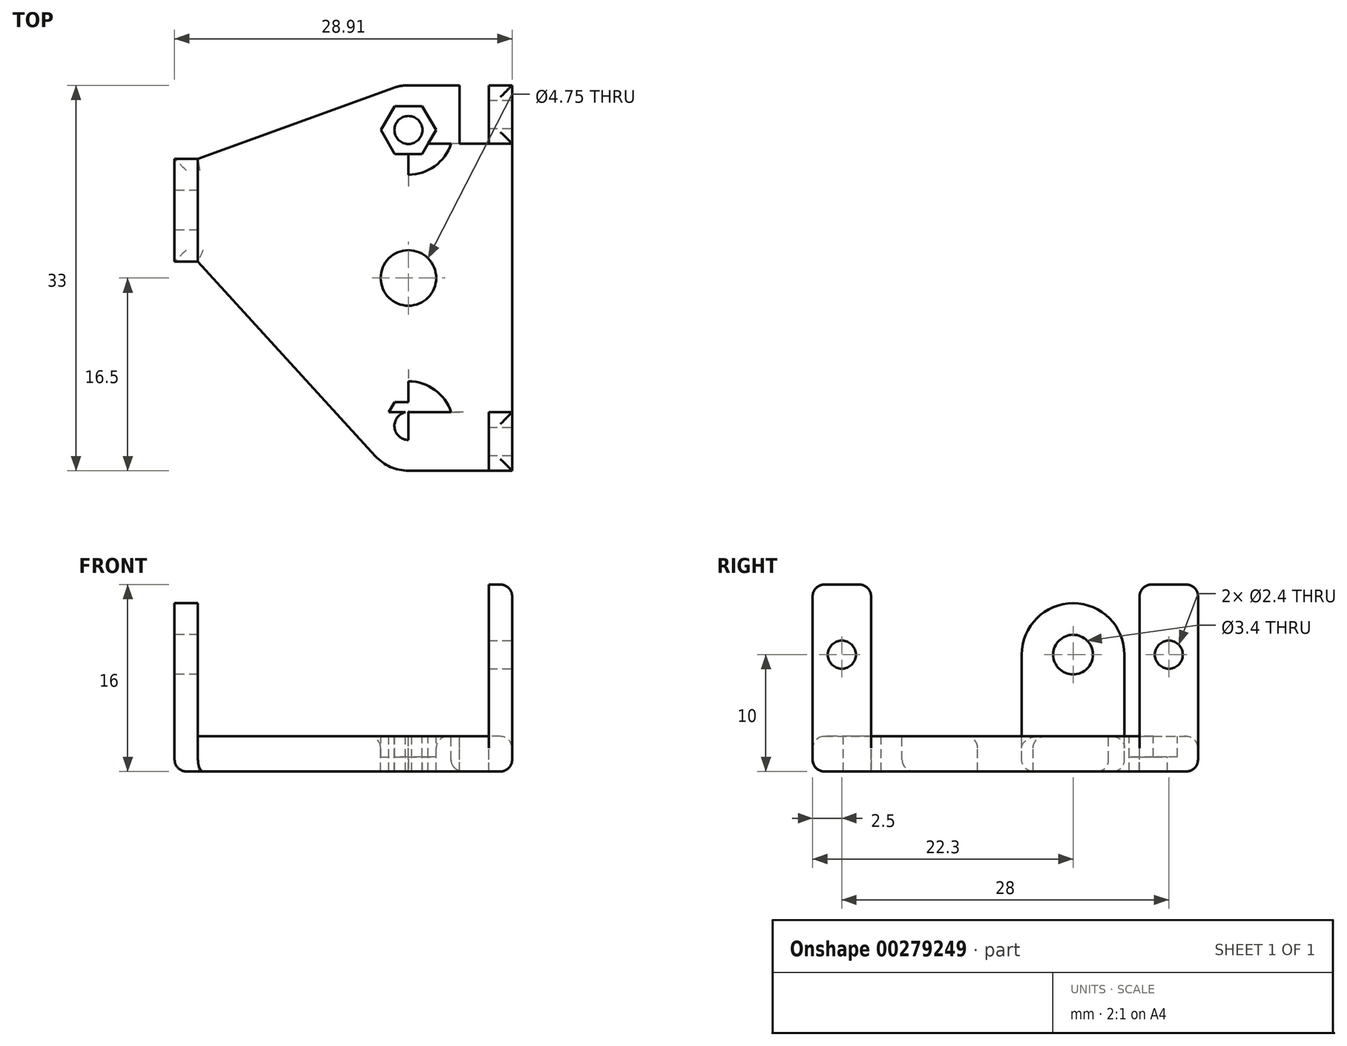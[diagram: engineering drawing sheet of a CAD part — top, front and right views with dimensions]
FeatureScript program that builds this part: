
annotation { "Feature Type Name" : "Feature", "Feature Type Description" : "" }
export const myFeature = defineFeature(function(context is Context, id is Id, definition is map)
    precondition{}
    {
        {
            var Q0;
            Q0=qCreatedBy(makeId("Top.planeOp"),FACE);
            var sketch = newSketch(context, id + "F0", { "sketchPlane" : qUnion([Q0])});
            skPoint(sketch, "E0.middle", {"position": v(0, 0) * mm});
            skCircle(sketch, "E1", {"center": v(0, 0) * mm, "radius": 2.38 * mm});
            skCircle(sketch, "E2", {"center": v(0, 12.67) * mm, "radius": 1.2 * mm});
            skCircle(sketch, "E3.MirrorC", {"center": v(0, -12.67) * mm, "radius": 1.2 * mm});
            skLineSegment(sketch, "E4.bottom", {"start": v(11.38, -11.5) * mm, "end": v(-11.38, -11.5) * mm});
            skLineSegment(sketch, "E4.top", {"start": v(11.38, 11.5) * mm, "end": v(-11.38, 11.5) * mm});
            skLineSegment(sketch, "E4.left", {"start": v(11.38, -11.5) * mm, "end": v(11.38, 11.5) * mm});
            skLineSegment(sketch, "E4.right", {"start": v(-11.38, -11.5) * mm, "end": v(-11.37, 11.5) * mm});
            skLineSegment(sketch, "E5.bottom", {"start": v(6.87, 11.5) * mm, "end": v(4.38, 11.5) * mm});
            skLineSegment(sketch, "E5.top", {"start": v(6.87, 16.5) * mm, "end": v(4.37, 16.5) * mm});
            skLineSegment(sketch, "E5.left", {"start": v(6.87, 11.5) * mm, "end": v(6.87, 16.5) * mm});
            skLineSegment(sketch, "E5.right", {"start": v(4.37, 11.5) * mm, "end": v(4.37, 16.5) * mm});
            skLineSegment(sketch, "E6.MirrorCS", {"start": v(4.38, -11.5) * mm, "end": v(4.38, -16.5) * mm});
            skLineSegment(sketch, "E7.MirrorCS", {"start": v(6.87, -11.5) * mm, "end": v(4.38, -11.5) * mm});
            skLineSegment(sketch, "E8.MirrorCS", {"start": v(6.88, -11.5) * mm, "end": v(6.88, -16.5) * mm});
            skLineSegment(sketch, "E9.MirrorCS", {"start": v(6.87, -16.5) * mm, "end": v(4.37, -16.5) * mm});
            skLineSegment(sketch, "E10.bottom", {"start": v(11.38, 11.5) * mm, "end": v(15.62, 11.5) * mm});
            skLineSegment(sketch, "E10.top", {"start": v(11.37, -0.5) * mm, "end": v(15.62, -0.5) * mm});
            skLineSegment(sketch, "E10.left", {"start": v(11.38, 11.5) * mm, "end": v(11.38, -0.5) * mm});
            skLineSegment(sketch, "E10.right", {"start": v(15.62, 11.5) * mm, "end": v(15.62, -0.5) * mm});
            skLineSegment(sketch, "E11.bottom", {"start": v(15.62, 8.1) * mm, "end": v(18.63, 8.1) * mm});
            skLineSegment(sketch, "E11.top", {"start": v(15.62, 3.5) * mm, "end": v(18.63, 3.5) * mm});
            skLineSegment(sketch, "E11.left", {"start": v(15.62, 8.1) * mm, "end": v(15.62, 3.5) * mm});
            skLineSegment(sketch, "E11.right", {"start": v(18.62, 8.1) * mm, "end": v(18.62, 3.5) * mm});
            skCircle(sketch, "E12.cCircle", {"center": v(0, 12.67) * mm, "radius": 2.05 * mm, "construction": true});
            skLineSegment(sketch, "E12.0", {"start": v(1.18, 10.62) * mm, "end": v(-1.18, 10.62) * mm});
            skLineSegment(sketch, "E12.1", {"start": v(-1.18, 10.62) * mm, "end": v(-2.37, 12.67) * mm});
            skLineSegment(sketch, "E12.2", {"start": v(-2.37, 12.67) * mm, "end": v(-1.18, 14.72) * mm});
            skLineSegment(sketch, "E12.3", {"start": v(-1.18, 14.72) * mm, "end": v(1.18, 14.72) * mm});
            skLineSegment(sketch, "E12.4", {"start": v(1.18, 14.72) * mm, "end": v(2.37, 12.67) * mm});
            skLineSegment(sketch, "E12.5", {"start": v(2.37, 12.67) * mm, "end": v(1.18, 10.62) * mm});
            skPoint(sketch, "E12.0.midPoint", {"position": v(0, 10.62) * mm});
            skCircle(sketch, "E13.MirrorC", {"center": v(0, -12.67) * mm, "radius": 2.05 * mm, "construction": true});
            skLineSegment(sketch, "E14.MirrorCS", {"start": v(1.18, -10.62) * mm, "end": v(-1.18, -10.62) * mm});
            skLineSegment(sketch, "E15.MirrorCS", {"start": v(2.37, -12.67) * mm, "end": v(1.18, -10.62) * mm});
            skLineSegment(sketch, "E16.MirrorCS", {"start": v(1.18, -14.72) * mm, "end": v(2.37, -12.67) * mm});
            skLineSegment(sketch, "E17.MirrorCS", {"start": v(-1.18, -14.72) * mm, "end": v(1.18, -14.72) * mm});
            skLineSegment(sketch, "E18.MirrorCS", {"start": v(-2.37, -12.67) * mm, "end": v(-1.18, -14.72) * mm});
            skLineSegment(sketch, "E19.MirrorCS", {"start": v(-1.18, -10.62) * mm, "end": v(-2.37, -12.67) * mm});
            skLineSegment(sketch, "E20.bottom", {"start": v(20.62, 24.4) * mm, "end": v(-20.62, 24.4) * mm});
            skLineSegment(sketch, "E20.top", {"start": v(20.62, 26.4) * mm, "end": v(-20.62, 26.4) * mm});
            skLineSegment(sketch, "E20.left", {"start": v(20.63, 24.4) * mm, "end": v(20.63, 26.4) * mm});
            skLineSegment(sketch, "E20.right", {"start": v(-20.63, 24.4) * mm, "end": v(-20.63, 26.4) * mm});
            skPoint(sketch, "E20.middle", {"position": v(0, 25.4) * mm});
            skLineSegment(sketch, "E21.bottom", {"start": v(22.62, 1.4) * mm, "end": v(20.62, 1.4) * mm});
            skLineSegment(sketch, "E21.top", {"start": v(22.62, 26.4) * mm, "end": v(20.62, 26.4) * mm});
            skLineSegment(sketch, "E21.left", {"start": v(22.62, 1.4) * mm, "end": v(22.62, 26.4) * mm});
            skLineSegment(sketch, "E21.right", {"start": v(20.62, 1.4) * mm, "end": v(20.62, 26.4) * mm});
            skLineSegment(sketch, "E22.MirrorCS", {"start": v(-22.62, 26.4) * mm, "end": v(-20.62, 26.4) * mm});
            skLineSegment(sketch, "E23.MirrorCS", {"start": v(-20.62, 1.4) * mm, "end": v(-20.62, 26.4) * mm});
            skLineSegment(sketch, "E24.MirrorCS", {"start": v(-22.62, 1.4) * mm, "end": v(-22.62, 26.4) * mm});
            skLineSegment(sketch, "E25.MirrorCS", {"start": v(-22.62, 1.4) * mm, "end": v(-20.62, 1.4) * mm});
            skCircle(sketch, "E26", {"center": v(0, 12.67) * mm, "radius": 3.83 * mm});
            skPoint(sketch, "E27.firstSnap0", {"position": v(0, 24.4) * mm});
            skLineSegment(sketch, "E27.bottom", {"start": v(0, 16.5) * mm, "end": v(8.87, 16.5) * mm});
            skLineSegment(sketch, "E27.top", {"start": v(0, -16.5) * mm, "end": v(8.88, -16.5) * mm});
            skLineSegment(sketch, "E27.left", {"start": v(0, 16.5) * mm, "end": v(0, -16.5) * mm});
            skLineSegment(sketch, "E27.right", {"start": v(8.87, 16.5) * mm, "end": v(8.88, -16.5) * mm});
            skCircle(sketch, "E28.MirrorC", {"center": v(0, -12.67) * mm, "radius": 3.83 * mm});
            skLineSegment(sketch, "E29.bottom", {"start": v(-20.62, 9.2) * mm, "end": v(-20.02, 9.2) * mm});
            skLineSegment(sketch, "E29.top", {"start": v(-20.62, 2.4) * mm, "end": v(-20.02, 2.4) * mm});
            skLineSegment(sketch, "E29.left", {"start": v(-20.62, 9.2) * mm, "end": v(-20.62, 2.4) * mm});
            skLineSegment(sketch, "E29.right", {"start": v(-20.02, 9.2) * mm, "end": v(-20.02, 2.4) * mm});
            skLineSegment(sketch, "E30.bottom", {"start": v(-18.02, 10.2) * mm, "end": v(-20.02, 10.2) * mm});
            skLineSegment(sketch, "E30.top", {"start": v(-18.02, 1.4) * mm, "end": v(-20.02, 1.4) * mm});
            skLineSegment(sketch, "E30.left", {"start": v(-18.02, 10.2) * mm, "end": v(-18.02, 1.4) * mm});
            skLineSegment(sketch, "E30.right", {"start": v(-20.02, 10.2) * mm, "end": v(-20.02, 1.4) * mm});
            skLineSegment(sketch, "E31", {"start": v(-18.02, 10.2) * mm, "end": v(-1.3, 16.27) * mm});
            skLineSegment(sketch, "E32", {"start": v(-18.02, 1.4) * mm, "end": v(-2.83, -15.25) * mm});
            skPoint(sketch, "E33.startSnap0", {"position": v(18.62, 5.8) * mm});
            skSolve(sketch);
        }
        {
            var Q0;
            {var subQ2=sQuery(id+"F0.wireOp",EDGE,"E30.bottom");Q0=makeQuery(id+"F0.imprint","IMPRINT",FACE,{"disambiguationData":[TD([[makeQuery(id+"F0.imprint","IMPRINT",EDGE,{"derivedFrom":subQ2}),1.0]])]});}
            var Q1;
            {var subQ0=sQuery(id+"F0.wireOp",EDGE,"E30.left");Q1=makeQuery(id+"F0.imprint","IMPRINT",FACE,{"disambiguationData":[TD([[makeQuery(id+"F0.imprint","IMPRINT",EDGE,{"derivedFrom":subQ0}),1.0]])]});}
            var Q2;
            {var subQ5=sQuery(id+"F0.wireOp",EDGE,"E27.left");var subQ6=sQuery(id+"F0.wireOp",EDGE,"E1");var subQ7=makeQuery(id+"F0.imprint","INTERSECT",VERTEX,{"disambiguationData":[OD(0.0)],"derivedFrom":[subQ6,subQ5]});Q2=makeQuery(id+"F0.imprint","IMPRINT",FACE,{"disambiguationData":[TD([[makeQuery(id+"F0.imprint","IMPRINT",EDGE,{"disambiguationData":[TD([[subQ7,-1.0]])],"derivedFrom":subQ6}),-1.0]])]});}
            var Q3;
            {var subQ0=sQuery(id+"F0.wireOp",EDGE,"E12.2");Q3=makeQuery(id+"F0.imprint","IMPRINT",FACE,{"disambiguationData":[TD([[makeQuery(id+"F0.imprint","IMPRINT",EDGE,{"derivedFrom":subQ0}),1.0]])]});}
            var Q4;
            {var subQ0=sQuery(id+"F0.wireOp",EDGE,"E12.1");var subQ3=sQuery(id+"F0.wireOp",EDGE,"E4.top");var subQ4=makeQuery(id+"F0.imprint","INTERSECT",VERTEX,{"derivedFrom":[subQ3,subQ0]});Q4=makeQuery(id+"F0.imprint","IMPRINT",FACE,{"disambiguationData":[TD([[makeQuery(id+"F0.imprint","IMPRINT",EDGE,{"disambiguationData":[TD([[subQ4,-1.0]])],"derivedFrom":subQ3}),1.0]])]});}
            var Q5;
            {var subQ0=sQuery(id+"F0.wireOp",EDGE,"E26");var subQ1=sQuery(id+"F0.wireOp",EDGE,"E4.top");var subQ2=makeQuery(id+"F0.imprint","INTERSECT",VERTEX,{"disambiguationData":[OD(0.0)],"derivedFrom":[subQ1,subQ0]});Q5=makeQuery(id+"F0.imprint","IMPRINT",FACE,{"disambiguationData":[TD([[makeQuery(id+"F0.imprint","IMPRINT",EDGE,{"disambiguationData":[TD([[subQ2,-1.0]])],"derivedFrom":subQ1}),1.0]])]});}
            var Q6;
            {var subQ1=sQuery(id+"F0.wireOp",EDGE,"E12.4");Q6=makeQuery(id+"F0.imprint","IMPRINT",FACE,{"disambiguationData":[TD([[makeQuery(id+"F0.imprint","IMPRINT",EDGE,{"derivedFrom":subQ1}),1.0]])]});}
            var Q7;
            {var subQ0=sQuery(id+"F0.wireOp",EDGE,"E5.right");Q7=makeQuery(id+"F0.imprint","IMPRINT",FACE,{"disambiguationData":[TD([[makeQuery(id+"F0.imprint","IMPRINT",EDGE,{"derivedFrom":subQ0}),1.0]])]});}
            var Q8;
            Q8=makeQuery(id+"F0.imprint","IMPRINT",FACE,{"disambiguationData":[TD([[makeQuery(id+"F0.imprint","IMPRINT",EDGE,{"derivedFrom":sQuery(id+"F0.wireOp",EDGE,"E5.bottom")}),-1.0]])]});
            var Q9;
            {var subQ0=sQuery(id+"F0.wireOp",EDGE,"E5.left");Q9=makeQuery(id+"F0.imprint","IMPRINT",FACE,{"disambiguationData":[TD([[makeQuery(id+"F0.imprint","IMPRINT",EDGE,{"derivedFrom":subQ0}),-1.0]])]});}
            var Q10;
            {var subQ10=sQuery(id+"F0.wireOp",EDGE,"E5.bottom");Q10=makeQuery(id+"F0.imprint","IMPRINT",FACE,{"disambiguationData":[TD([[makeQuery(id+"F0.imprint","IMPRINT",EDGE,{"derivedFrom":subQ10}),1.0]])]});}
            var Q11;
            {var subQ0=sQuery(id+"F0.wireOp",EDGE,"E6.MirrorCS");Q11=makeQuery(id+"F0.imprint","IMPRINT",FACE,{"disambiguationData":[TD([[makeQuery(id+"F0.imprint","IMPRINT",EDGE,{"derivedFrom":subQ0}),-1.0]])]});}
            var Q12;
            {var subQ0=sQuery(id+"F0.wireOp",EDGE,"E6.MirrorCS");Q12=makeQuery(id+"F0.imprint","IMPRINT",FACE,{"disambiguationData":[TD([[makeQuery(id+"F0.imprint","IMPRINT",EDGE,{"derivedFrom":subQ0}),1.0]])]});}
            var Q13;
            {var subQ0=sQuery(id+"F0.wireOp",EDGE,"E8.MirrorCS");Q13=makeQuery(id+"F0.imprint","IMPRINT",FACE,{"disambiguationData":[TD([[makeQuery(id+"F0.imprint","IMPRINT",EDGE,{"derivedFrom":subQ0}),1.0]])]});}
            var Q14;
            {var subQ0=sQuery(id+"F0.wireOp",EDGE,"E32");var subQ1=sQuery(id+"F0.wireOp",EDGE,"E4.bottom");var subQ2=makeQuery(id+"F0.imprint","INTERSECT",VERTEX,{"derivedFrom":[subQ1,subQ0]});Q14=makeQuery(id+"F0.imprint","IMPRINT",FACE,{"disambiguationData":[TD([[makeQuery(id+"F0.imprint","IMPRINT",EDGE,{"disambiguationData":[TD([[subQ2,1.0]])],"derivedFrom":subQ1}),1.0]])]});}
            var Q15;
            {var subQ0=sQuery(id+"F0.wireOp",EDGE,"E18.MirrorCS");Q15=makeQuery(id+"F0.imprint","IMPRINT",FACE,{"disambiguationData":[TD([[makeQuery(id+"F0.imprint","IMPRINT",EDGE,{"derivedFrom":subQ0}),-1.0]])]});}
            var Q16;
            {var subQ1=sQuery(id+"F0.wireOp",EDGE,"E16.MirrorCS");Q16=makeQuery(id+"F0.imprint","IMPRINT",FACE,{"disambiguationData":[TD([[makeQuery(id+"F0.imprint","IMPRINT",EDGE,{"derivedFrom":subQ1}),-1.0]])]});}
            var Q17;
            {var subQ5=sQuery(id+"F0.wireOp",EDGE,"E4.bottom");var subQ7=sQuery(id+"F0.wireOp",EDGE,"E19.MirrorCS");var subQ9=makeQuery(id+"F0.imprint","INTERSECT",VERTEX,{"derivedFrom":[subQ5,subQ7]});Q17=makeQuery(id+"F0.imprint","IMPRINT",FACE,{"disambiguationData":[TD([[makeQuery(id+"F0.imprint","IMPRINT",EDGE,{"disambiguationData":[TD([[subQ9,-1.0]])],"derivedFrom":subQ5}),-1.0]])]});}
            var Q18;
            {var subQ3=sQuery(id+"F0.wireOp",EDGE,"E28.MirrorC");var subQ7=sQuery(id+"F0.wireOp",EDGE,"E4.bottom");var subQ9=makeQuery(id+"F0.imprint","INTERSECT",VERTEX,{"disambiguationData":[OD(0.0)],"derivedFrom":[subQ7,subQ3]});Q18=makeQuery(id+"F0.imprint","IMPRINT",FACE,{"disambiguationData":[TD([[makeQuery(id+"F0.imprint","IMPRINT",EDGE,{"disambiguationData":[TD([[subQ9,-1.0]])],"derivedFrom":subQ7}),-1.0]])]});}
            var Q19;
            {var subQ0=sQuery(id+"F0.wireOp",EDGE,"E12.2");Q19=makeQuery(id+"F0.imprint","IMPRINT",FACE,{"disambiguationData":[TD([[makeQuery(id+"F0.imprint","IMPRINT",EDGE,{"derivedFrom":subQ0}),-1.0]])]});}
            var Q20;
            {var subQ0=sQuery(id+"F0.wireOp",EDGE,"E12.4");Q20=makeQuery(id+"F0.imprint","IMPRINT",FACE,{"disambiguationData":[TD([[makeQuery(id+"F0.imprint","IMPRINT",EDGE,{"derivedFrom":subQ0}),-1.0]])]});}
            var Q21;
            {var subQ5=sQuery(id+"F0.wireOp",EDGE,"E2");var subQ7=sQuery(id+"F0.wireOp",EDGE,"E27.left");var subQ9=makeQuery(id+"F0.imprint","INTERSECT",VERTEX,{"disambiguationData":[OD(1.0)],"derivedFrom":[subQ5,subQ7]});Q21=makeQuery(id+"F0.imprint","IMPRINT",FACE,{"disambiguationData":[TD([[makeQuery(id+"F0.imprint","IMPRINT",EDGE,{"disambiguationData":[TD([[subQ9,-1.0]])],"derivedFrom":subQ5}),-1.0]])]});}
            var Q22;
            {var subQ3=sQuery(id+"F0.wireOp",EDGE,"E4.top");var subQ7=sQuery(id+"F0.wireOp",EDGE,"E2");var subQ8=makeQuery(id+"F0.imprint","INTERSECT",VERTEX,{"disambiguationData":[OD(0.0)],"derivedFrom":[subQ7,subQ3]});Q22=makeQuery(id+"F0.imprint","IMPRINT",FACE,{"disambiguationData":[TD([[makeQuery(id+"F0.imprint","IMPRINT",EDGE,{"disambiguationData":[TD([[subQ8,-1.0]])],"derivedFrom":subQ7}),-1.0]])]});}
            var Q23;
            {var subQ0=sQuery(id+"F0.wireOp",EDGE,"E18.MirrorCS");Q23=makeQuery(id+"F0.imprint","IMPRINT",FACE,{"disambiguationData":[TD([[makeQuery(id+"F0.imprint","IMPRINT",EDGE,{"derivedFrom":subQ0}),1.0]])]});}
            var Q24;
            {var subQ5=sQuery(id+"F0.wireOp",EDGE,"E4.bottom");var subQ7=sQuery(id+"F0.wireOp",EDGE,"E3.MirrorC");var subQ8=makeQuery(id+"F0.imprint","INTERSECT",VERTEX,{"disambiguationData":[OD(0.0)],"derivedFrom":[subQ7,subQ5]});Q24=makeQuery(id+"F0.imprint","IMPRINT",FACE,{"disambiguationData":[TD([[makeQuery(id+"F0.imprint","IMPRINT",EDGE,{"disambiguationData":[TD([[subQ8,-1.0]])],"derivedFrom":subQ7}),1.0]])]});}
            var Q25;
            {var subQ0=sQuery(id+"F0.wireOp",EDGE,"E16.MirrorCS");Q25=makeQuery(id+"F0.imprint","IMPRINT",FACE,{"disambiguationData":[TD([[makeQuery(id+"F0.imprint","IMPRINT",EDGE,{"derivedFrom":subQ0}),1.0]])]});}
            var Q26;
            {var subQ5=sQuery(id+"F0.wireOp",EDGE,"E27.left");var subQ7=sQuery(id+"F0.wireOp",EDGE,"E3.MirrorC");var subQ8=makeQuery(id+"F0.imprint","INTERSECT",VERTEX,{"disambiguationData":[OD(1.0)],"derivedFrom":[subQ7,subQ5]});Q26=makeQuery(id+"F0.imprint","IMPRINT",FACE,{"disambiguationData":[TD([[makeQuery(id+"F0.imprint","IMPRINT",EDGE,{"disambiguationData":[TD([[subQ8,-1.0]])],"derivedFrom":subQ7}),1.0]])]});}
            extrude(context, id + "F1", {"entities" : qUnion([Q0, Q1, Q2, Q3, Q4, Q5, Q6, Q7, Q8, Q9, Q10, Q11, Q12, Q13, Q14, Q15, Q16, Q17, Q18, Q19, Q20, Q21, Q22, Q23, Q24, Q25, Q26]), "oppositeDirection" : true, "depth" : 3 * mm});
        }
        {
            var Q0;
            Q0=makeQuery(id+"F1.opExtrude","CAP_FACE",FACE,{"disambiguationData":[OSD([sQuery(id+"F0.wireOp",EDGE,"E1"),sQuery(id+"F0.wireOp",EDGE,"E2"),sQuery(id+"F0.wireOp",EDGE,"E3.MirrorC"),sQuery(id+"F0.wireOp",EDGE,"E26"),sQuery(id+"F0.wireOp",EDGE,"E27.bottom"),sQuery(id+"F0.wireOp",EDGE,"E27.top"),sQuery(id+"F0.wireOp",EDGE,"E27.right"),sQuery(id+"F0.wireOp",EDGE,"E28.MirrorC"),sQuery(id+"F0.wireOp",EDGE,"E30.bottom"),sQuery(id+"F0.wireOp",EDGE,"E30.top"),sQuery(id+"F0.wireOp",EDGE,"E30.right"),sQuery(id+"F0.wireOp",EDGE,"E31"),sQuery(id+"F0.wireOp",EDGE,"E32")])],"isStart":true});
            var sketch = newSketch(context, id + "F2", { "sketchPlane" : qUnion([Q0])});
            skCircle(sketch, "E34.cCircle", {"center": v(0, 12.67) * mm, "radius": 2.05 * mm, "construction": true});
            skLineSegment(sketch, "E34.0", {"start": v(1.18, 10.62) * mm, "end": v(-1.18, 10.62) * mm});
            skLineSegment(sketch, "E34.1", {"start": v(-1.18, 10.62) * mm, "end": v(-2.37, 12.67) * mm});
            skLineSegment(sketch, "E34.2", {"start": v(-2.37, 12.67) * mm, "end": v(-1.18, 14.72) * mm});
            skLineSegment(sketch, "E34.3", {"start": v(-1.18, 14.72) * mm, "end": v(1.18, 14.72) * mm});
            skLineSegment(sketch, "E34.4", {"start": v(1.18, 14.72) * mm, "end": v(2.37, 12.67) * mm});
            skLineSegment(sketch, "E34.5", {"start": v(2.37, 12.67) * mm, "end": v(1.18, 10.62) * mm});
            skPoint(sketch, "E34.0.midPoint", {"position": v(0, 10.62) * mm});
            skLineSegment(sketch, "E35.MirrorCS", {"start": v(-1.18, -10.62) * mm, "end": v(-2.37, -12.67) * mm});
            skLineSegment(sketch, "E36.MirrorCS", {"start": v(-2.37, -12.67) * mm, "end": v(-1.18, -14.72) * mm});
            skLineSegment(sketch, "E37.MirrorCS", {"start": v(-1.18, -14.72) * mm, "end": v(1.18, -14.72) * mm});
            skLineSegment(sketch, "E38.MirrorCS", {"start": v(1.18, -14.72) * mm, "end": v(2.37, -12.67) * mm});
            skLineSegment(sketch, "E39.MirrorCS", {"start": v(2.37, -12.67) * mm, "end": v(1.18, -10.62) * mm});
            skLineSegment(sketch, "E40.MirrorCS", {"start": v(1.18, -10.62) * mm, "end": v(-1.18, -10.62) * mm});
            skCircle(sketch, "E41.MirrorC", {"center": v(0, -12.67) * mm, "radius": 2.05 * mm, "construction": true});
            skSolve(sketch);
        }
        {
            var Q0;
            Q0=makeQuery(id+"F2.imprint","IMPRINT",FACE,{"disambiguationData":[TD([[makeQuery(id+"F2.imprint","IMPRINT",EDGE,{"derivedFrom":sQuery(id+"F2.wireOp",EDGE,"E34.0")}),-1.0]])]});
            var Q1;
            Q1=makeQuery(id+"F2.imprint","IMPRINT",FACE,{"disambiguationData":[TD([[makeQuery(id+"F2.imprint","IMPRINT",EDGE,{"derivedFrom":sQuery(id+"F2.wireOp",EDGE,"E35.MirrorCS")}),1.0]])]});
            extrude(context, id + "F3", {"entities" : qUnion([Q0, Q1]), "operationType" : NewBodyOperationType.REMOVE, "oppositeDirection" : true, "depth" : 1.75 * mm});
        }
        {
            var Q0;
            Q0=makeQuery(id+"F1.opExtrude","SWEPT_FACE",FACE,{"disambiguationData":[OSD([sQuery(id+"F0.wireOp",EDGE,"E30.right")])]});
            var sketch = newSketch(context, id + "F4", { "sketchPlane" : qUnion([Q0])});
            skCircle(sketch, "E42", {"center": v(-5.8, 7) * mm, "radius": 1.7 * mm});
            skLineSegment(sketch, "E43.bottom", {"start": v(-1.4, -3) * mm, "end": v(-10.2, -3) * mm});
            skLineSegment(sketch, "E43.top", {"start": v(-1.4, 7) * mm, "end": v(-10.2, 7) * mm});
            skLineSegment(sketch, "E43.left", {"start": v(-1.4, -3) * mm, "end": v(-1.4, 7) * mm});
            skLineSegment(sketch, "E43.right", {"start": v(-10.2, -3) * mm, "end": v(-10.2, 7) * mm});
            skCircle(sketch, "E44", {"center": v(-5.8, 7) * mm, "radius": 4.4 * mm});
            skSolve(sketch);
        }
        {
            var Q0;
            {var subQ3=sQuery(id+"F4.wireOp",EDGE,"E43.bottom");Q0=makeQuery(id+"F4.imprint","IMPRINT",FACE,{"disambiguationData":[TD([[makeQuery(id+"F4.imprint","IMPRINT",EDGE,{"derivedFrom":subQ3}),1.0]])]});}
            var Q1;
            {var subQ0=sQuery(id+"F4.wireOp",EDGE,"E43.right");var subQ1=makeQuery(id+"F1.opExtrude","CAP_EDGE",EDGE,{"disambiguationData":[OSD([sQuery(id+"F0.wireOp",EDGE,"E30.right")])],"isStart":true});var subQ2=makeQuery(id+"F4.imprint","INTERSECT",VERTEX,{"derivedFrom":[subQ1,subQ0]});Q1=makeQuery(id+"F4.imprint","IMPRINT",FACE,{"disambiguationData":[TD([[makeQuery(id+"F4.imprint","IMPRINT",EDGE,{"disambiguationData":[TD([[subQ2,-1.0]])],"derivedFrom":subQ1}),1.0]])]});}
            var Q2;
            {var subQ0=sQuery(id+"F4.wireOp",EDGE,"E43.left");var subQ1=makeQuery(id+"F1.opExtrude","CAP_EDGE",EDGE,{"disambiguationData":[OSD([sQuery(id+"F0.wireOp",EDGE,"E30.right")])],"isStart":true});var subQ2=makeQuery(id+"F4.imprint","INTERSECT",VERTEX,{"derivedFrom":[subQ1,subQ0]});Q2=makeQuery(id+"F4.imprint","IMPRINT",FACE,{"disambiguationData":[TD([[makeQuery(id+"F4.imprint","IMPRINT",EDGE,{"disambiguationData":[TD([[subQ2,1.0]])],"derivedFrom":subQ1}),1.0]])]});}
            var Q3;
            {var subQ0=sQuery(id+"F4.wireOp",EDGE,"E44");var subQ1=makeQuery(id+"F1.opExtrude","CAP_EDGE",EDGE,{"disambiguationData":[OSD([sQuery(id+"F0.wireOp",EDGE,"E30.right")])],"isStart":true});var subQ2=makeQuery(id+"F4.imprint","INTERSECT",VERTEX,{"disambiguationData":[OD(0.0)],"derivedFrom":[subQ1,subQ0]});Q3=makeQuery(id+"F4.imprint","IMPRINT",FACE,{"disambiguationData":[TD([[makeQuery(id+"F4.imprint","IMPRINT",EDGE,{"disambiguationData":[TD([[subQ2,-1.0]])],"derivedFrom":subQ0}),1.0]])]});}
            var Q4;
            {var subQ1=sQuery(id+"F4.wireOp",EDGE,"E43.top");var subQ3=sQuery(id+"F4.wireOp",EDGE,"E42");var subQ9=makeQuery(id+"F4.imprint","INTERSECT",VERTEX,{"disambiguationData":[OD(0.0)],"derivedFrom":[subQ3,subQ1]});Q4=makeQuery(id+"F4.imprint","IMPRINT",FACE,{"disambiguationData":[TD([[makeQuery(id+"F4.imprint","IMPRINT",EDGE,{"disambiguationData":[TD([[subQ9,1.0]])],"derivedFrom":subQ3}),-1.0]])]});}
            var Q5;
            {var subQ0=sQuery(id+"F4.wireOp",EDGE,"E43.top");var subQ1=sQuery(id+"F4.wireOp",EDGE,"E42");var subQ2=makeQuery(id+"F4.imprint","INTERSECT",VERTEX,{"disambiguationData":[OD(0.0)],"derivedFrom":[subQ1,subQ0]});Q5=makeQuery(id+"F4.imprint","IMPRINT",FACE,{"disambiguationData":[TD([[makeQuery(id+"F4.imprint","IMPRINT",EDGE,{"disambiguationData":[TD([[subQ2,-1.0]])],"derivedFrom":subQ1}),-1.0]])]});}
            extrude(context, id + "F5", {"entities" : qUnion([Q0, Q1, Q2, Q3, Q4, Q5]), "operationType" : NewBodyOperationType.ADD, "oppositeDirection" : true, "depth" : 2 * mm});
        }
        {
            var Q0;
            Q0=makeQuery(id+"F1.opExtrude","CAP_FACE",FACE,{"disambiguationData":[OSD([sQuery(id+"F0.wireOp",EDGE,"E1"),sQuery(id+"F0.wireOp",EDGE,"E2"),sQuery(id+"F0.wireOp",EDGE,"E3.MirrorC"),sQuery(id+"F0.wireOp",EDGE,"E26"),sQuery(id+"F0.wireOp",EDGE,"E27.bottom"),sQuery(id+"F0.wireOp",EDGE,"E27.top"),sQuery(id+"F0.wireOp",EDGE,"E27.right"),sQuery(id+"F0.wireOp",EDGE,"E28.MirrorC"),sQuery(id+"F0.wireOp",EDGE,"E30.bottom"),sQuery(id+"F0.wireOp",EDGE,"E30.top"),sQuery(id+"F0.wireOp",EDGE,"E30.right"),sQuery(id+"F0.wireOp",EDGE,"E31"),sQuery(id+"F0.wireOp",EDGE,"E32")])],"isStart":true});
            var sketch = newSketch(context, id + "F6", { "sketchPlane" : qUnion([Q0])});
            skLineSegment(sketch, "E45.bottom", {"start": v(8.87, 16.5) * mm, "end": v(6.87, 16.5) * mm});
            skLineSegment(sketch, "E45.top", {"start": v(8.88, 11.5) * mm, "end": v(6.87, 11.5) * mm});
            skLineSegment(sketch, "E45.left", {"start": v(8.87, 16.5) * mm, "end": v(8.87, 11.5) * mm});
            skLineSegment(sketch, "E45.right", {"start": v(6.87, 16.5) * mm, "end": v(6.87, 11.5) * mm});
            skLineSegment(sketch, "E46.MirrorCS", {"start": v(8.87, -16.5) * mm, "end": v(6.87, -16.5) * mm});
            skLineSegment(sketch, "E47.MirrorCS", {"start": v(8.87, -16.5) * mm, "end": v(8.87, -11.5) * mm});
            skLineSegment(sketch, "E48.MirrorCS", {"start": v(8.88, -11.5) * mm, "end": v(6.87, -11.5) * mm});
            skLineSegment(sketch, "E49.MirrorCS", {"start": v(6.87, -16.5) * mm, "end": v(6.87, -11.5) * mm});
            skSolve(sketch);
        }
        {
            var Q0;
            Q0=makeQuery(id+"F6.imprint","IMPRINT",FACE,{"disambiguationData":[TD([[makeQuery(id+"F6.imprint","IMPRINT",EDGE,{"derivedFrom":sQuery(id+"F6.wireOp",EDGE,"E45.bottom")}),-1.0]])]});
            var Q1;
            Q1=makeQuery(id+"F6.imprint","IMPRINT",FACE,{"disambiguationData":[TD([[makeQuery(id+"F6.imprint","IMPRINT",EDGE,{"derivedFrom":sQuery(id+"F6.wireOp",EDGE,"E46.MirrorCS")}),1.0]])]});
            extrude(context, id + "F7", {"entities" : qUnion([Q0, Q1]), "operationType" : NewBodyOperationType.ADD, "depth" : 13 * mm});
        }
        {
            var Q0;
            Q0=makeQuery(id+"F7.boolean.opBoolean","MERGE",FACE,{"derivedFrom":[makeQuery(id+"F1.opExtrude","SWEPT_FACE",FACE,{"disambiguationData":[OSD([sQuery(id+"F0.wireOp",EDGE,"E27.right")])]}),makeQuery(id+"F7.opExtrude","SWEPT_FACE",FACE,{"disambiguationData":[OSD([sQuery(id+"F6.wireOp",EDGE,"E45.left")])]}),makeQuery(id+"F7.opExtrude","SWEPT_FACE",FACE,{"disambiguationData":[OSD([sQuery(id+"F6.wireOp",EDGE,"E47.MirrorCS")])]})]});
            var sketch = newSketch(context, id + "F8", { "sketchPlane" : qUnion([Q0])});
            skCircle(sketch, "E50", {"center": v(-14, 7) * mm, "radius": 1.2 * mm});
            skCircle(sketch, "E51.MirrorC", {"center": v(14, 7) * mm, "radius": 1.2 * mm});
            skSolve(sketch);
        }
        {
            var Q0;
            Q0=makeQuery(id+"F1.opExtrude","CAP_EDGE",EDGE,{"disambiguationData":[OSD([sQuery(id+"F0.wireOp",EDGE,"E27.right")])],"isStart":true});
            var Q1;
            Q1=makeQuery(id+"F1.opExtrude","CAP_EDGE",EDGE,{"disambiguationData":[OSD([sQuery(id+"F0.wireOp",EDGE,"E27.right")])],"isStart":false});
            var Q2;
            Q2=makeQuery(id+"F1.opExtrude","CAP_EDGE",EDGE,{"disambiguationData":[OSD([sQuery(id+"F0.wireOp",EDGE,"E27.bottom")])],"isStart":false});
            var Q3;
            Q3=makeQuery(id+"F1.opExtrude","CAP_EDGE",EDGE,{"disambiguationData":[OSD([sQuery(id+"F0.wireOp",EDGE,"E30.right")])],"isStart":false});
            var Q4;
            Q4=makeQuery(id+"F1.opExtrude","CAP_EDGE",EDGE,{"disambiguationData":[OSD([sQuery(id+"F0.wireOp",EDGE,"E30.bottom")])],"isStart":false});
            var Q5;
            Q5=makeQuery(id+"F1.opExtrude","CAP_EDGE",EDGE,{"disambiguationData":[OSD([sQuery(id+"F0.wireOp",EDGE,"E30.top")])],"isStart":false});
            var Q6;
            Q6=makeQuery(id+"F1.opExtrude","CAP_EDGE",EDGE,{"disambiguationData":[OSD([sQuery(id+"F0.wireOp",EDGE,"E32")])],"isStart":false});
            var Q7;
            Q7=makeQuery(id+"F1.opExtrude","CAP_EDGE",EDGE,{"disambiguationData":[OSD([sQuery(id+"F0.wireOp",EDGE,"E28.MirrorC")])],"isStart":false});
            var Q8;
            Q8=makeQuery(id+"F1.opExtrude","CAP_EDGE",EDGE,{"disambiguationData":[OSD([sQuery(id+"F0.wireOp",EDGE,"E27.top")])],"isStart":false});
            var Q9;
            Q9=makeQuery(id+"F1.opExtrude","CAP_EDGE",EDGE,{"disambiguationData":[OSD([sQuery(id+"F0.wireOp",EDGE,"E31")])],"isStart":false});
            var Q10;
            Q10=makeQuery(id+"F1.opExtrude","CAP_EDGE",EDGE,{"disambiguationData":[OSD([sQuery(id+"F0.wireOp",EDGE,"E26")])],"isStart":false});
            var Q11;
            Q11=makeQuery(id+"F1.opExtrude","CAP_EDGE",EDGE,{"disambiguationData":[OSD([sQuery(id+"F0.wireOp",EDGE,"E32")])],"isStart":true});
            var Q12;
            Q12=makeQuery(id+"F1.opExtrude","CAP_EDGE",EDGE,{"disambiguationData":[OSD([sQuery(id+"F0.wireOp",EDGE,"E31")])],"isStart":true});
            var Q13;
            Q13=makeQuery(id+"F1.opExtrude","CAP_EDGE",EDGE,{"disambiguationData":[OSD([sQuery(id+"F0.wireOp",EDGE,"E1")])],"isStart":true});
            var Q14;
            Q14=makeQuery(id+"F7.opExtrude","CAP_EDGE",EDGE,{"disambiguationData":[OSD([sQuery(id+"F6.wireOp",EDGE,"E47.MirrorCS")])],"isStart":false});
            var Q15;
            Q15=makeQuery(id+"F7.opExtrude","CAP_EDGE",EDGE,{"disambiguationData":[OSD([sQuery(id+"F6.wireOp",EDGE,"E45.left")])],"isStart":false});
            var Q16;
            Q16=makeQuery(id+"F7.opExtrude","CAP_EDGE",EDGE,{"disambiguationData":[OSD([sQuery(id+"F6.wireOp",EDGE,"E46.MirrorCS")])],"isStart":false});
            var Q17;
            Q17=makeQuery(id+"F7.opExtrude","CAP_EDGE",EDGE,{"disambiguationData":[OSD([sQuery(id+"F6.wireOp",EDGE,"E45.top")])],"isStart":false});
            var Q18;
            Q18=makeQuery(id+"F7.opExtrude","CAP_EDGE",EDGE,{"disambiguationData":[OSD([sQuery(id+"F6.wireOp",EDGE,"E48.MirrorCS")])],"isStart":false});
            var Q19;
            Q19=makeQuery(id+"F7.opExtrude","CAP_EDGE",EDGE,{"disambiguationData":[OSD([sQuery(id+"F6.wireOp",EDGE,"E45.bottom")])],"isStart":false});
            fillet(context, id + "F9", {"entities" : qUnion([Q0, Q1, Q2, Q3, Q4, Q5, Q6, Q7, Q8, Q9, Q10, Q11, Q12, Q13, Q14, Q15, Q16, Q17, Q18, Q19]), "radius" : 1 * mm, "tangentPropagation" : true, "allowEdgeOverflow" : false});
        }
        {
            var Q0;
            Q0=sQuery(id+"F8.wireOp",VERTEX,"E50.center");
            var Q1;
            Q1=sQuery(id+"F8.wireOp",VERTEX,"E51.MirrorC.center");
            var Q2;
            Q2=makeQuery(id+"F1.opExtrude","SWEPT_BODY",BODY,{"disambiguationData":[OSD([sQuery(id+"F0.wireOp",EDGE,"E1"),sQuery(id+"F0.wireOp",EDGE,"E2"),sQuery(id+"F0.wireOp",EDGE,"E3.MirrorC"),sQuery(id+"F0.wireOp",EDGE,"E26"),sQuery(id+"F0.wireOp",EDGE,"E27.bottom"),sQuery(id+"F0.wireOp",EDGE,"E27.top"),sQuery(id+"F0.wireOp",EDGE,"E27.right"),sQuery(id+"F0.wireOp",EDGE,"E28.MirrorC"),sQuery(id+"F0.wireOp",EDGE,"E30.bottom"),sQuery(id+"F0.wireOp",EDGE,"E30.top"),sQuery(id+"F0.wireOp",EDGE,"E30.right"),sQuery(id+"F0.wireOp",EDGE,"E31"),sQuery(id+"F0.wireOp",EDGE,"E32")])]});
            hole(context, id + "F10", {"style" : HoleStyle.SIMPLE, "endStyle" : HoleEndStyle.THROUGH, "holeDiameter" : 2.4 * mm, "tappedDepth" : 12 * mm, "tapClearance" : 3, "locations" : qUnion([Q0, Q1]), "scope" : qUnion([Q2])});
        }
    });
